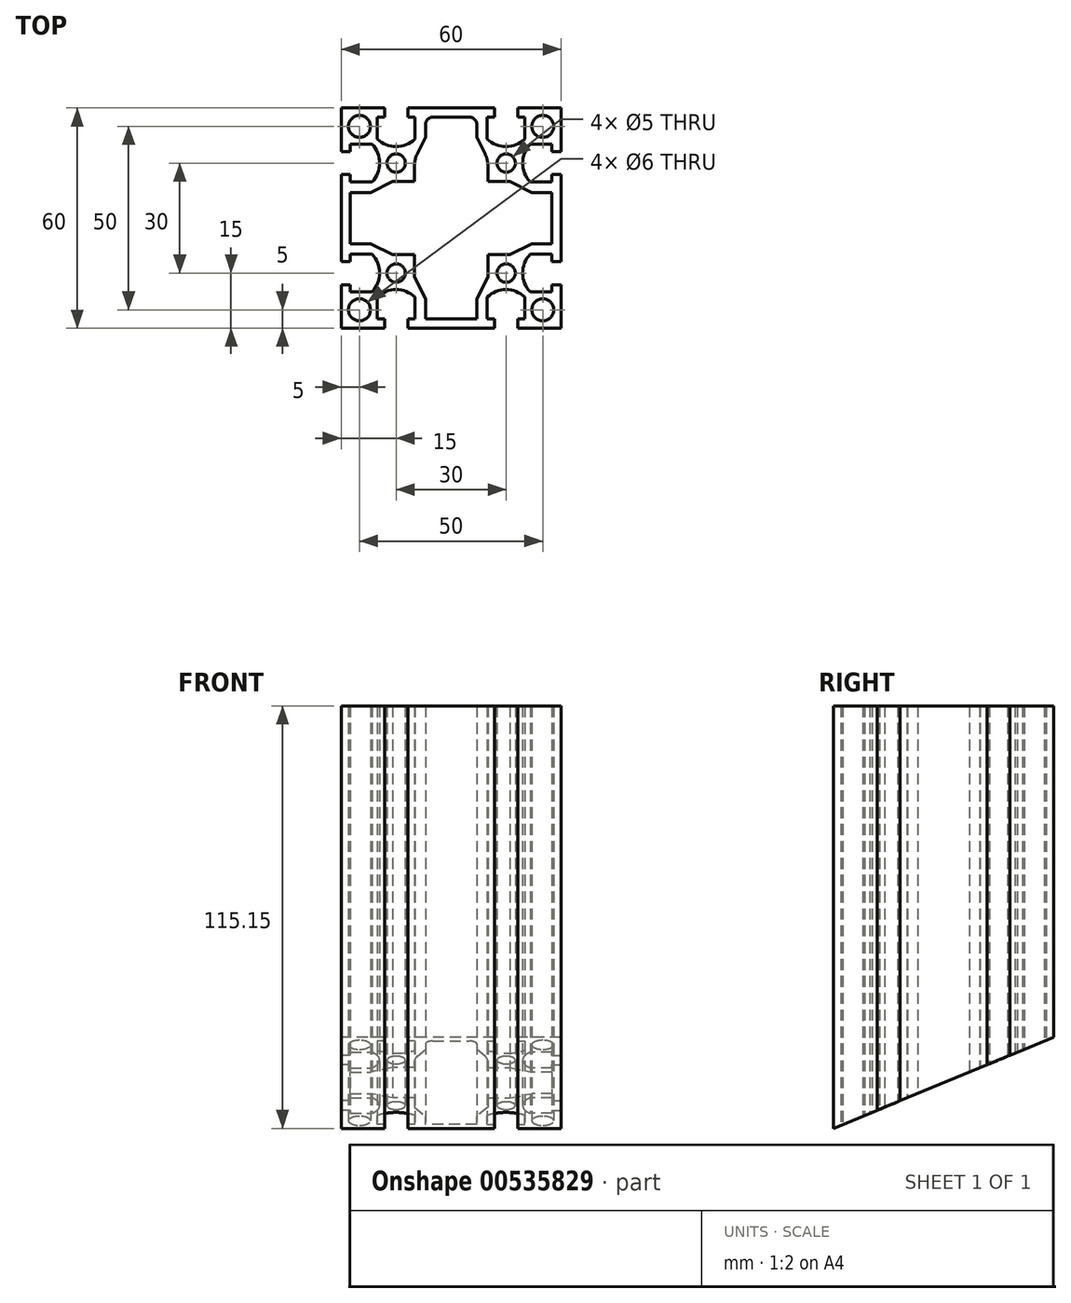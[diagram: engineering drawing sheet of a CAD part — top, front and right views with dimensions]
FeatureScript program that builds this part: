
annotation { "Feature Type Name" : "Feature", "Feature Type Description" : "" }
export const myFeature = defineFeature(function(context is Context, id is Id, definition is map)
    precondition{}
    {
        {
            var Q0;
            Q0=qCreatedBy(makeId("Top.planeOp"),FACE);
            var sketch = newSketch(context, id + "F0", { "sketchPlane" : qUnion([Q0])});
            skLineSegment(sketch, "E0.bottom", {"start": v(30, -30) * mm, "end": v(-30, -30) * mm});
            skLineSegment(sketch, "E0.top", {"start": v(30, 30) * mm, "end": v(-30, 30) * mm});
            skLineSegment(sketch, "E0.left", {"start": v(30, -30) * mm, "end": v(30, 30) * mm});
            skLineSegment(sketch, "E0.right", {"start": v(-30, -30) * mm, "end": v(-30, 30) * mm});
            skPoint(sketch, "E0.middle", {"position": v(0, 0) * mm});
            skLineSegment(sketch, "E1.top", {"start": v(-11.85, 30) * mm, "end": v(-18.15, 30) * mm});
            skLineSegment(sketch, "E1.left", {"start": v(-11.85, 27.5) * mm, "end": v(-11.85, 30) * mm});
            skLineSegment(sketch, "E1.right", {"start": v(-18.15, 27.5) * mm, "end": v(-18.15, 30) * mm});
            skPoint(sketch, "E1.middle", {"position": v(-15, 28.75) * mm});
            skLineSegment(sketch, "E2.bottom", {"start": v(-9.85, 27.5) * mm, "end": v(-11.85, 27.5) * mm});
            skLineSegment(sketch, "E2.left", {"start": v(-9.85, 27.5) * mm, "end": v(-9.85, 21.55) * mm});
            skLineSegment(sketch, "E2.right", {"start": v(-20.15, 27.5) * mm, "end": v(-20.15, 21.55) * mm});
            skPoint(sketch, "E2.middle", {"position": v(-15, 24.52) * mm});
            skArc(sketch, "E3", {"start": v(-20.15, 21.55) * mm, "mid": v(-15, 19.5) * mm, "end": v(-9.85, 21.55) * mm});
            skPoint(sketch, "E4.MirrorP", {"position": v(15, 24.52) * mm});
            skPoint(sketch, "E5.MirrorP", {"position": v(15, 28.75) * mm});
            skLineSegment(sketch, "E6.MirrorCS", {"start": v(11.85, 27.5) * mm, "end": v(11.85, 30) * mm});
            skLineSegment(sketch, "E7.MirrorCS", {"start": v(18.15, 27.5) * mm, "end": v(18.15, 30) * mm});
            skLineSegment(sketch, "E8.MirrorCS", {"start": v(9.85, 27.5) * mm, "end": v(11.85, 27.5) * mm});
            skLineSegment(sketch, "E9.MirrorCS", {"start": v(9.85, 27.5) * mm, "end": v(9.85, 21.55) * mm});
            skArc(sketch, "E10.MirrorCS", {"start": v(20.15, 21.55) * mm, "mid": v(15, 19.5) * mm, "end": v(9.85, 21.55) * mm});
            skLineSegment(sketch, "E11.MirrorCS", {"start": v(20.15, 27.5) * mm, "end": v(20.15, 21.55) * mm});
            skLineSegment(sketch, "E12.MirrorCS", {"start": v(11.85, 30) * mm, "end": v(18.15, 30) * mm});
            skLineSegment(sketch, "E13.1.0", {"start": v(27.5, 20.15) * mm, "end": v(21.55, 20.15) * mm});
            skLineSegment(sketch, "E13.1.1", {"start": v(27.5, 9.85) * mm, "end": v(21.55, 9.85) * mm});
            skArc(sketch, "E13.1.2", {"start": v(21.55, 20.15) * mm, "mid": v(19.5, 15) * mm, "end": v(21.55, 9.85) * mm});
            skLineSegment(sketch, "E13.1.3", {"start": v(27.5, -9.85) * mm, "end": v(21.55, -9.85) * mm});
            skLineSegment(sketch, "E13.1.4", {"start": v(27.5, -20.15) * mm, "end": v(21.55, -20.15) * mm});
            skPoint(sketch, "E13.1.5", {"position": v(28.75, 15) * mm});
            skPoint(sketch, "E13.1.6", {"position": v(28.75, -15) * mm});
            skArc(sketch, "E13.1.7", {"start": v(21.55, -20.15) * mm, "mid": v(19.5, -15) * mm, "end": v(21.55, -9.85) * mm});
            skPoint(sketch, "E13.1.8", {"position": v(24.52, -15) * mm});
            skPoint(sketch, "E13.1.9", {"position": v(24.52, 15) * mm});
            skLineSegment(sketch, "E13.1.10", {"start": v(27.5, 9.85) * mm, "end": v(27.5, 20.15) * mm});
            skLineSegment(sketch, "E13.1.11", {"start": v(27.5, -11.85) * mm, "end": v(27.5, -18.15) * mm});
            skLineSegment(sketch, "E13.1.12", {"start": v(30, 11.85) * mm, "end": v(30, 18.15) * mm});
            skLineSegment(sketch, "E13.1.13", {"start": v(30, -11.85) * mm, "end": v(30, -18.15) * mm});
            skLineSegment(sketch, "E13.1.14", {"start": v(27.5, 18.15) * mm, "end": v(30, 18.15) * mm});
            skLineSegment(sketch, "E13.1.15", {"start": v(27.5, 11.85) * mm, "end": v(30, 11.85) * mm});
            skLineSegment(sketch, "E13.1.16", {"start": v(27.5, 11.85) * mm, "end": v(27.5, 18.15) * mm});
            skLineSegment(sketch, "E13.1.17", {"start": v(27.5, -9.85) * mm, "end": v(27.5, -20.15) * mm});
            skLineSegment(sketch, "E13.1.18", {"start": v(27.5, -18.15) * mm, "end": v(30, -18.15) * mm});
            skLineSegment(sketch, "E13.1.19", {"start": v(27.5, -11.85) * mm, "end": v(30, -11.85) * mm});
            skLineSegment(sketch, "E13.2.0", {"start": v(20.15, -27.5) * mm, "end": v(20.15, -21.55) * mm});
            skLineSegment(sketch, "E13.2.1", {"start": v(9.85, -27.5) * mm, "end": v(9.85, -21.55) * mm});
            skArc(sketch, "E13.2.2", {"start": v(20.15, -21.55) * mm, "mid": v(15, -19.5) * mm, "end": v(9.85, -21.55) * mm});
            skLineSegment(sketch, "E13.2.3", {"start": v(-9.85, -27.5) * mm, "end": v(-9.85, -21.55) * mm});
            skLineSegment(sketch, "E13.2.4", {"start": v(-20.15, -27.5) * mm, "end": v(-20.15, -21.55) * mm});
            skPoint(sketch, "E13.2.5", {"position": v(15, -28.75) * mm});
            skPoint(sketch, "E13.2.6", {"position": v(-15, -28.75) * mm});
            skArc(sketch, "E13.2.7", {"start": v(-20.15, -21.55) * mm, "mid": v(-15, -19.5) * mm, "end": v(-9.85, -21.55) * mm});
            skPoint(sketch, "E13.2.8", {"position": v(-15, -24.52) * mm});
            skPoint(sketch, "E13.2.9", {"position": v(15, -24.52) * mm});
            skLineSegment(sketch, "E13.2.10", {"start": v(9.85, -27.5) * mm, "end": v(20.15, -27.5) * mm});
            skLineSegment(sketch, "E13.2.11", {"start": v(-11.85, -27.5) * mm, "end": v(-18.15, -27.5) * mm});
            skLineSegment(sketch, "E13.2.12", {"start": v(11.85, -30) * mm, "end": v(18.15, -30) * mm});
            skLineSegment(sketch, "E13.2.13", {"start": v(-11.85, -30) * mm, "end": v(-18.15, -30) * mm});
            skLineSegment(sketch, "E13.2.14", {"start": v(18.15, -27.5) * mm, "end": v(18.15, -30) * mm});
            skLineSegment(sketch, "E13.2.15", {"start": v(11.85, -27.5) * mm, "end": v(11.85, -30) * mm});
            skLineSegment(sketch, "E13.2.16", {"start": v(11.85, -27.5) * mm, "end": v(18.15, -27.5) * mm});
            skLineSegment(sketch, "E13.2.17", {"start": v(-9.85, -27.5) * mm, "end": v(-20.15, -27.5) * mm});
            skLineSegment(sketch, "E13.2.18", {"start": v(-18.15, -27.5) * mm, "end": v(-18.15, -30) * mm});
            skLineSegment(sketch, "E13.2.19", {"start": v(-11.85, -27.5) * mm, "end": v(-11.85, -30) * mm});
            skLineSegment(sketch, "E13.3.0", {"start": v(-27.5, -20.15) * mm, "end": v(-21.55, -20.15) * mm});
            skLineSegment(sketch, "E13.3.1", {"start": v(-27.5, -9.85) * mm, "end": v(-21.55, -9.85) * mm});
            skArc(sketch, "E13.3.2", {"start": v(-21.55, -20.15) * mm, "mid": v(-19.5, -15) * mm, "end": v(-21.55, -9.85) * mm});
            skLineSegment(sketch, "E13.3.3", {"start": v(-27.5, 9.85) * mm, "end": v(-21.55, 9.85) * mm});
            skLineSegment(sketch, "E13.3.4", {"start": v(-27.5, 20.15) * mm, "end": v(-21.55, 20.15) * mm});
            skPoint(sketch, "E13.3.5", {"position": v(-28.75, -15) * mm});
            skPoint(sketch, "E13.3.6", {"position": v(-28.75, 15) * mm});
            skArc(sketch, "E13.3.7", {"start": v(-21.55, 20.15) * mm, "mid": v(-19.5, 15) * mm, "end": v(-21.55, 9.85) * mm});
            skPoint(sketch, "E13.3.8", {"position": v(-24.52, 15) * mm});
            skPoint(sketch, "E13.3.9", {"position": v(-24.52, -15) * mm});
            skLineSegment(sketch, "E13.3.10", {"start": v(-27.5, -9.85) * mm, "end": v(-27.5, -20.15) * mm});
            skLineSegment(sketch, "E13.3.11", {"start": v(-27.5, 11.85) * mm, "end": v(-27.5, 18.15) * mm});
            skLineSegment(sketch, "E13.3.12", {"start": v(-30, -11.85) * mm, "end": v(-30, -18.15) * mm});
            skLineSegment(sketch, "E13.3.13", {"start": v(-30, 11.85) * mm, "end": v(-30, 18.15) * mm});
            skLineSegment(sketch, "E13.3.14", {"start": v(-27.5, -18.15) * mm, "end": v(-30, -18.15) * mm});
            skLineSegment(sketch, "E13.3.15", {"start": v(-27.5, -11.85) * mm, "end": v(-30, -11.85) * mm});
            skLineSegment(sketch, "E13.3.16", {"start": v(-27.5, -11.85) * mm, "end": v(-27.5, -18.15) * mm});
            skLineSegment(sketch, "E13.3.17", {"start": v(-27.5, 9.85) * mm, "end": v(-27.5, 20.15) * mm});
            skLineSegment(sketch, "E13.3.18", {"start": v(-27.5, 18.15) * mm, "end": v(-30, 18.15) * mm});
            skLineSegment(sketch, "E13.3.19", {"start": v(-27.5, 11.85) * mm, "end": v(-30, 11.85) * mm});
            skLineSegment(sketch, "E13.anchor1", {"start": v(0, 0) * mm, "end": v(-20.15, 21.55) * mm, "construction": true});
            skLineSegment(sketch, "E13.anchor2", {"start": v(0, 0) * mm, "end": v(-21.55, -20.15) * mm, "construction": true});
            skLineSegment(sketch, "E14.trimOffspring", {"start": v(-18.15, 27.5) * mm, "end": v(-20.15, 27.5) * mm});
            skLineSegment(sketch, "E15.trimOffspring", {"start": v(18.15, 27.5) * mm, "end": v(20.15, 27.5) * mm});
            skCircle(sketch, "E16", {"center": v(-15, 15) * mm, "radius": 2.5 * mm});
            skCircle(sketch, "E17", {"center": v(-25, 25) * mm, "radius": 3 * mm});
            skCircle(sketch, "E18.MirrorC", {"center": v(25, 25) * mm, "radius": 3 * mm});
            skCircle(sketch, "E19.MirrorC", {"center": v(25, -25) * mm, "radius": 3 * mm});
            skCircle(sketch, "E20.MirrorC", {"center": v(-25, -25) * mm, "radius": 3 * mm});
            skCircle(sketch, "E21.MirrorC", {"center": v(15, 15) * mm, "radius": 2.5 * mm});
            skCircle(sketch, "E22.MirrorC", {"center": v(15, -15) * mm, "radius": 2.5 * mm});
            skCircle(sketch, "E23.MirrorC", {"center": v(-15, -15) * mm, "radius": 2.5 * mm});
            skLineSegment(sketch, "E24", {"start": v(-7, 27.5) * mm, "end": v(0, 27.5) * mm});
            skLineSegment(sketch, "E25", {"start": v(-7, 27.5) * mm, "end": v(-7, 22) * mm});
            skLineSegment(sketch, "E26", {"start": v(-10, 10) * mm, "end": v(-10, 16) * mm});
            skLineSegment(sketch, "E27", {"start": v(-10, 16) * mm, "end": v(-7, 22) * mm});
            skLineSegment(sketch, "E28.MirrorCS", {"start": v(10, 10) * mm, "end": v(10, 16) * mm});
            skLineSegment(sketch, "E29.MirrorCS", {"start": v(10, 16) * mm, "end": v(7, 22) * mm});
            skLineSegment(sketch, "E30.MirrorCS", {"start": v(7, 27.5) * mm, "end": v(0, 27.5) * mm});
            skLineSegment(sketch, "E31.MirrorCS", {"start": v(7, 27.5) * mm, "end": v(7, 22) * mm});
            skLineSegment(sketch, "E32.1.0", {"start": v(-10, -10) * mm, "end": v(-16, -10) * mm});
            skLineSegment(sketch, "E32.1.1", {"start": v(-16, -10) * mm, "end": v(-22, -7) * mm});
            skLineSegment(sketch, "E32.1.2", {"start": v(-27.5, -7) * mm, "end": v(-22, -7) * mm});
            skLineSegment(sketch, "E32.1.3", {"start": v(-27.5, -7) * mm, "end": v(-27.5, 0) * mm});
            skLineSegment(sketch, "E32.1.4", {"start": v(-27.5, 7) * mm, "end": v(-27.5, 0) * mm});
            skLineSegment(sketch, "E32.1.5", {"start": v(-27.5, 7) * mm, "end": v(-22, 7) * mm});
            skLineSegment(sketch, "E32.1.6", {"start": v(-16, 10) * mm, "end": v(-22, 7) * mm});
            skLineSegment(sketch, "E32.1.7", {"start": v(-10, 10) * mm, "end": v(-16, 10) * mm});
            skLineSegment(sketch, "E32.2.0", {"start": v(10, -10) * mm, "end": v(10, -16) * mm});
            skLineSegment(sketch, "E32.2.1", {"start": v(10, -16) * mm, "end": v(7, -22) * mm});
            skLineSegment(sketch, "E32.2.2", {"start": v(7, -27.5) * mm, "end": v(7, -22) * mm});
            skLineSegment(sketch, "E32.2.3", {"start": v(7, -27.5) * mm, "end": v(0, -27.5) * mm});
            skLineSegment(sketch, "E32.2.4", {"start": v(-7, -27.5) * mm, "end": v(0, -27.5) * mm});
            skLineSegment(sketch, "E32.2.5", {"start": v(-7, -27.5) * mm, "end": v(-7, -22) * mm});
            skLineSegment(sketch, "E32.2.6", {"start": v(-10, -16) * mm, "end": v(-7, -22) * mm});
            skLineSegment(sketch, "E32.2.7", {"start": v(-10, -10) * mm, "end": v(-10, -16) * mm});
            skLineSegment(sketch, "E32.3.0", {"start": v(10, 10) * mm, "end": v(16, 10) * mm});
            skLineSegment(sketch, "E32.3.1", {"start": v(16, 10) * mm, "end": v(22, 7) * mm});
            skLineSegment(sketch, "E32.3.2", {"start": v(27.5, 7) * mm, "end": v(22, 7) * mm});
            skLineSegment(sketch, "E32.3.3", {"start": v(27.5, 7) * mm, "end": v(27.5, 0) * mm});
            skLineSegment(sketch, "E32.3.4", {"start": v(27.5, -7) * mm, "end": v(27.5, 0) * mm});
            skLineSegment(sketch, "E32.3.5", {"start": v(27.5, -7) * mm, "end": v(22, -7) * mm});
            skLineSegment(sketch, "E32.3.6", {"start": v(16, -10) * mm, "end": v(22, -7) * mm});
            skLineSegment(sketch, "E32.3.7", {"start": v(10, -10) * mm, "end": v(16, -10) * mm});
            skSolve(sketch);
        }
        {
            var Q0;
            {var subQ30=sQuery(id+"F0.wireOp",EDGE,"E1.left");Q0=makeQuery(id+"F0.imprint","IMPRINT",FACE,{"disambiguationData":[TD([[makeQuery(id+"F0.imprint","IMPRINT",EDGE,{"derivedFrom":subQ30}),-1.0]])]});}
            extrude(context, id + "F1", {"entities" : qUnion([Q0]), "depth" : 140 * mm, "offsetDistance" : 25 * mm});
        }
        {
            var Q0;
            Q0=makeQuery(id+"F1.opExtrude","SWEPT_EDGE",EDGE,{"disambiguationData":[OSD([sQuery(id+"F0.wireOp",EDGE,"E24"),sQuery(id+"F0.wireOp",EDGE,"E25")])]});
            var Q1;
            Q1=makeQuery(id+"F1.opExtrude","SWEPT_EDGE",EDGE,{"disambiguationData":[OSD([sQuery(id+"F0.wireOp",EDGE,"E30.MirrorCS"),sQuery(id+"F0.wireOp",EDGE,"E31.MirrorCS")])]});
            var Q2;
            Q2=makeQuery(id+"F1.opExtrude","SWEPT_EDGE",EDGE,{"disambiguationData":[OSD([sQuery(id+"F0.wireOp",EDGE,"840db5bc-c403-45cd-90c7-254e62d9e8c5.3.2"),sQuery(id+"F0.wireOp",EDGE,"840db5bc-c403-45cd-90c7-254e62d9e8c5.3.3")])]});
            var Q3;
            Q3=makeQuery(id+"F1.opExtrude","SWEPT_EDGE",EDGE,{"disambiguationData":[OSD([sQuery(id+"F0.wireOp",EDGE,"840db5bc-c403-45cd-90c7-254e62d9e8c5.3.4"),sQuery(id+"F0.wireOp",EDGE,"840db5bc-c403-45cd-90c7-254e62d9e8c5.3.5")])]});
            var Q4;
            Q4=makeQuery(id+"F1.opExtrude","SWEPT_EDGE",EDGE,{"disambiguationData":[OSD([sQuery(id+"F0.wireOp",EDGE,"840db5bc-c403-45cd-90c7-254e62d9e8c5.1.4"),sQuery(id+"F0.wireOp",EDGE,"840db5bc-c403-45cd-90c7-254e62d9e8c5.1.5")])]});
            var Q5;
            Q5=makeQuery(id+"F1.opExtrude","SWEPT_EDGE",EDGE,{"disambiguationData":[OSD([sQuery(id+"F0.wireOp",EDGE,"840db5bc-c403-45cd-90c7-254e62d9e8c5.1.2"),sQuery(id+"F0.wireOp",EDGE,"840db5bc-c403-45cd-90c7-254e62d9e8c5.1.3")])]});
            var Q6;
            Q6=makeQuery(id+"F1.opExtrude","SWEPT_EDGE",EDGE,{"disambiguationData":[OSD([sQuery(id+"F0.wireOp",EDGE,"840db5bc-c403-45cd-90c7-254e62d9e8c5.2.2"),sQuery(id+"F0.wireOp",EDGE,"840db5bc-c403-45cd-90c7-254e62d9e8c5.2.3")])]});
            var Q7;
            Q7=makeQuery(id+"F1.opExtrude","SWEPT_EDGE",EDGE,{"disambiguationData":[OSD([sQuery(id+"F0.wireOp",EDGE,"840db5bc-c403-45cd-90c7-254e62d9e8c5.2.4"),sQuery(id+"F0.wireOp",EDGE,"840db5bc-c403-45cd-90c7-254e62d9e8c5.2.5")])]});
            fillet(context, id + "F2", {"entities" : qUnion([Q0, Q1, Q2, Q3, Q4, Q5, Q6, Q7]), "radius" : 2 * mm, "tangentPropagation" : true, "allowEdgeOverflow" : false});
        }
        {
            var Q0;
            Q0=makeQuery(id+"F1.opExtrude","SWEPT_EDGE",EDGE,{"disambiguationData":[OSD([sQuery(id+"F0.wireOp",EDGE,"E26"),sQuery(id+"F0.wireOp",EDGE,"E27")])]});
            var Q1;
            Q1=makeQuery(id+"F1.opExtrude","SWEPT_EDGE",EDGE,{"disambiguationData":[OSD([sQuery(id+"F0.wireOp",EDGE,"E28.MirrorCS"),sQuery(id+"F0.wireOp",EDGE,"E29.MirrorCS")])]});
            var Q2;
            Q2=makeQuery(id+"F1.opExtrude","SWEPT_EDGE",EDGE,{"disambiguationData":[OSD([sQuery(id+"F0.wireOp",EDGE,"840db5bc-c403-45cd-90c7-254e62d9e8c5.3.0"),sQuery(id+"F0.wireOp",EDGE,"840db5bc-c403-45cd-90c7-254e62d9e8c5.3.1")])]});
            var Q3;
            Q3=makeQuery(id+"F1.opExtrude","SWEPT_EDGE",EDGE,{"disambiguationData":[OSD([sQuery(id+"F0.wireOp",EDGE,"840db5bc-c403-45cd-90c7-254e62d9e8c5.1.6"),sQuery(id+"F0.wireOp",EDGE,"840db5bc-c403-45cd-90c7-254e62d9e8c5.1.7")])]});
            var Q4;
            Q4=makeQuery(id+"F1.opExtrude","SWEPT_EDGE",EDGE,{"disambiguationData":[OSD([sQuery(id+"F0.wireOp",EDGE,"840db5bc-c403-45cd-90c7-254e62d9e8c5.1.0"),sQuery(id+"F0.wireOp",EDGE,"840db5bc-c403-45cd-90c7-254e62d9e8c5.1.1")])]});
            var Q5;
            Q5=makeQuery(id+"F1.opExtrude","SWEPT_EDGE",EDGE,{"disambiguationData":[OSD([sQuery(id+"F0.wireOp",EDGE,"840db5bc-c403-45cd-90c7-254e62d9e8c5.3.6"),sQuery(id+"F0.wireOp",EDGE,"840db5bc-c403-45cd-90c7-254e62d9e8c5.3.7")])]});
            var Q6;
            Q6=makeQuery(id+"F1.opExtrude","SWEPT_EDGE",EDGE,{"disambiguationData":[OSD([sQuery(id+"F0.wireOp",EDGE,"840db5bc-c403-45cd-90c7-254e62d9e8c5.2.0"),sQuery(id+"F0.wireOp",EDGE,"840db5bc-c403-45cd-90c7-254e62d9e8c5.2.1")])]});
            var Q7;
            Q7=makeQuery(id+"F1.opExtrude","SWEPT_EDGE",EDGE,{"disambiguationData":[OSD([sQuery(id+"F0.wireOp",EDGE,"840db5bc-c403-45cd-90c7-254e62d9e8c5.2.6"),sQuery(id+"F0.wireOp",EDGE,"840db5bc-c403-45cd-90c7-254e62d9e8c5.2.7")])]});
            fillet(context, id + "F3", {"entities" : qUnion([Q0, Q1, Q2, Q3, Q4, Q5, Q6, Q7]), "radius" : 7 * mm, "tangentPropagation" : true, "allowEdgeOverflow" : false});
        }
        {
            var Q0;
            {var subQ0=sQuery(id+"F0.wireOp",EDGE,"E0.bottom");Q0=makeQuery(id+"F1.opExtrude","SWEPT_FACE",FACE,{"disambiguationData":[OSD([subQ0]),TDD([makeQuery(id+"F0.imprint","IMPRINT",EDGE,{"disambiguationData":[TD([[makeQuery(id+"F0.imprint","INTERSECT",VERTEX,{"derivedFrom":[subQ0,sQuery(id+"F0.wireOp",EDGE,"E13.2.12"),sQuery(id+"F0.wireOp",EDGE,"E13.2.15")]}),-1.0]])],"derivedFrom":subQ0})])]});}
            var sketch = newSketch(context, id + "F4", { "sketchPlane" : qUnion([Q0])});
            skLineSegment(sketch, "E33.0", {"start": v(-18.15, 140) * mm, "end": v(-30, 140) * mm});
            skLineSegment(sketch, "E33.1", {"start": v(30, 140) * mm, "end": v(30, 0) * mm});
            skLineSegment(sketch, "E34", {"start": v(-30, 140) * mm, "end": v(30, 140) * mm});
            skLineSegment(sketch, "E35", {"start": v(30, 80) * mm, "end": v(-30, 140) * mm});
            skLineSegment(sketch, "E36.0", {"start": v(-18.15, 0) * mm, "end": v(-30, 0) * mm});
            skLineSegment(sketch, "E37", {"start": v(-30, 0) * mm, "end": v(30, 0) * mm});
            skLineSegment(sketch, "E38", {"start": v(30, 60) * mm, "end": v(-30, 0) * mm});
            skSolve(sketch);
        }
        {
            var Q0;
            Q0=qCreatedBy(makeId("Right.planeOp"),FACE);
            var sketch = newSketch(context, id + "F5", { "sketchPlane" : qUnion([Q0])});
            skLineSegment(sketch, "E39.bottom", {"start": v(130.97, 66.67) * mm, "end": v(-30, 0) * mm});
            skLineSegment(sketch, "E39.top", {"start": v(214.6, -135.23) * mm, "end": v(53.63, -201.9) * mm});
            skLineSegment(sketch, "E39.left", {"start": v(130.97, 66.67) * mm, "end": v(214.6, -135.23) * mm});
            skLineSegment(sketch, "E39.right", {"start": v(-30, 0) * mm, "end": v(53.63, -201.9) * mm});
            skLineSegment(sketch, "E40.bottom", {"start": v(-2, 217.27) * mm, "end": v(-162.34, 150.86) * mm});
            skLineSegment(sketch, "E40.top", {"start": v(30, 140) * mm, "end": v(-130.33, 73.59) * mm});
            skLineSegment(sketch, "E40.left", {"start": v(-2, 217.27) * mm, "end": v(30, 140) * mm});
            skLineSegment(sketch, "E40.right", {"start": v(-162.34, 150.86) * mm, "end": v(-130.33, 73.59) * mm});
            skSolve(sketch);
        }
        {
            var Q0;
            Q0=makeQuery(id+"F5.imprint","IMPRINT",FACE,{"disambiguationData":[TD([[makeQuery(id+"F5.imprint","IMPRINT",EDGE,{"derivedFrom":sQuery(id+"F5.wireOp",EDGE,"E39.bottom")}),1.0]])]});
            var Q1;
            Q1=makeQuery(id+"F5.imprint","IMPRINT",FACE,{"disambiguationData":[TD([[makeQuery(id+"F5.imprint","IMPRINT",EDGE,{"derivedFrom":sQuery(id+"F5.wireOp",EDGE,"E40.bottom")}),1.0]])]});
            extrude(context, id + "F6", {"entities" : qUnion([Q0, Q1]), "operationType" : NewBodyOperationType.REMOVE, "oppositeDirection" : true, "depth" : 30 * mm, "offsetDistance" : 25 * mm, "hasSecondDirection" : true, "secondDirectionOppositeDirection" : false, "secondDirectionDepth" : 30 * mm});
        }
        {
            var Q0;
            Q0=qCreatedBy(makeId("Right.planeOp"),FACE);
            var sketch = newSketch(context, id + "F7", { "sketchPlane" : qUnion([Q0])});
            skLineSegment(sketch, "E41.bottom", {"start": v(101.16, 165.85) * mm, "end": v(-30, 165.85) * mm});
            skLineSegment(sketch, "E41.top", {"start": v(101.16, 115.15) * mm, "end": v(-30, 115.15) * mm});
            skLineSegment(sketch, "E41.left", {"start": v(101.16, 165.85) * mm, "end": v(101.16, 115.15) * mm});
            skLineSegment(sketch, "E41.right", {"start": v(-30, 165.85) * mm, "end": v(-30, 115.15) * mm});
            skSolve(sketch);
        }
        {
            var Q0;
            Q0 = qSketchRegion(id + "F7", true);
            extrude(context, id + "F8", {"entities" : qUnion([Q0]), "operationType" : NewBodyOperationType.REMOVE, "depth" : 30 * mm, "offsetDistance" : 25 * mm, "hasSecondDirection" : true, "secondDirectionOppositeDirection" : true, "secondDirectionDepth" : 30 * mm});
        }
    });
